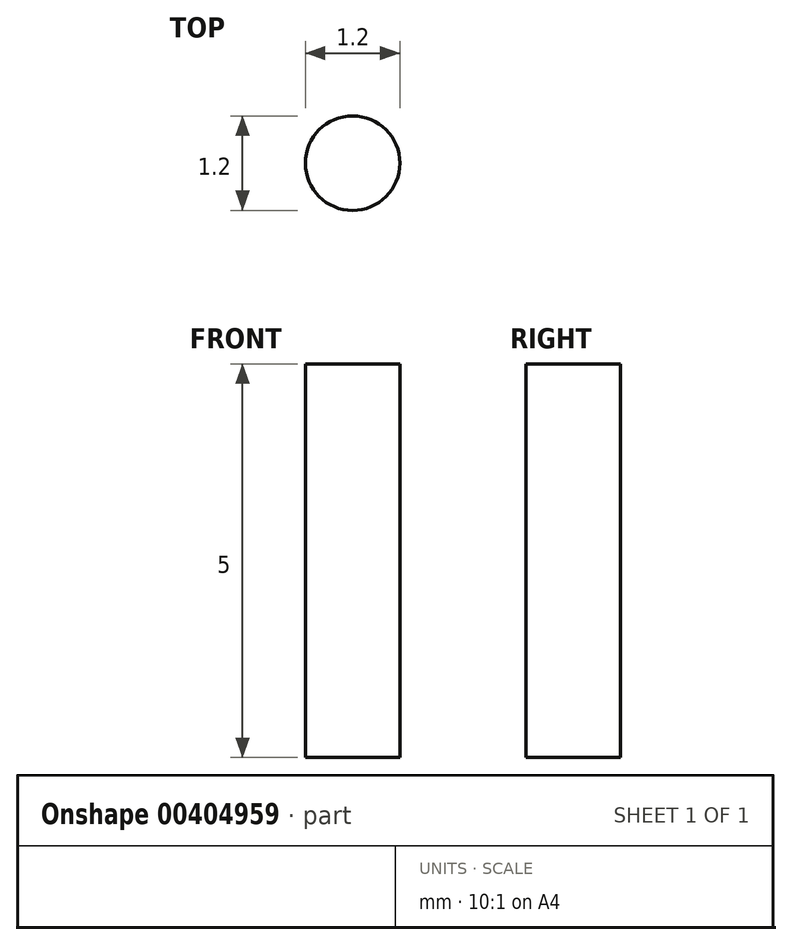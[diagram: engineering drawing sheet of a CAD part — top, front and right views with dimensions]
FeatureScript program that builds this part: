
annotation { "Feature Type Name" : "Feature", "Feature Type Description" : "" }
export const myFeature = defineFeature(function(context is Context, id is Id, definition is map)
    precondition{}
    {
        {
            var Q0;
            Q0=qCreatedBy(makeId("Top.planeOp"),FACE);
            var sketch = newSketch(context, id + "F0", { "sketchPlane" : qUnion([Q0])});
            skCircle(sketch, "E0", {"center": v(0, 0) * mm, "radius": 0.6 * mm});
            skSolve(sketch);
        }
        {
            var Q0;
            Q0=qSketchRegion(id+"F0",true);
            extrude(context, id + "F1", {"entities" : qUnion([Q0]), "depth" : 5 * mm});
        }
    });
